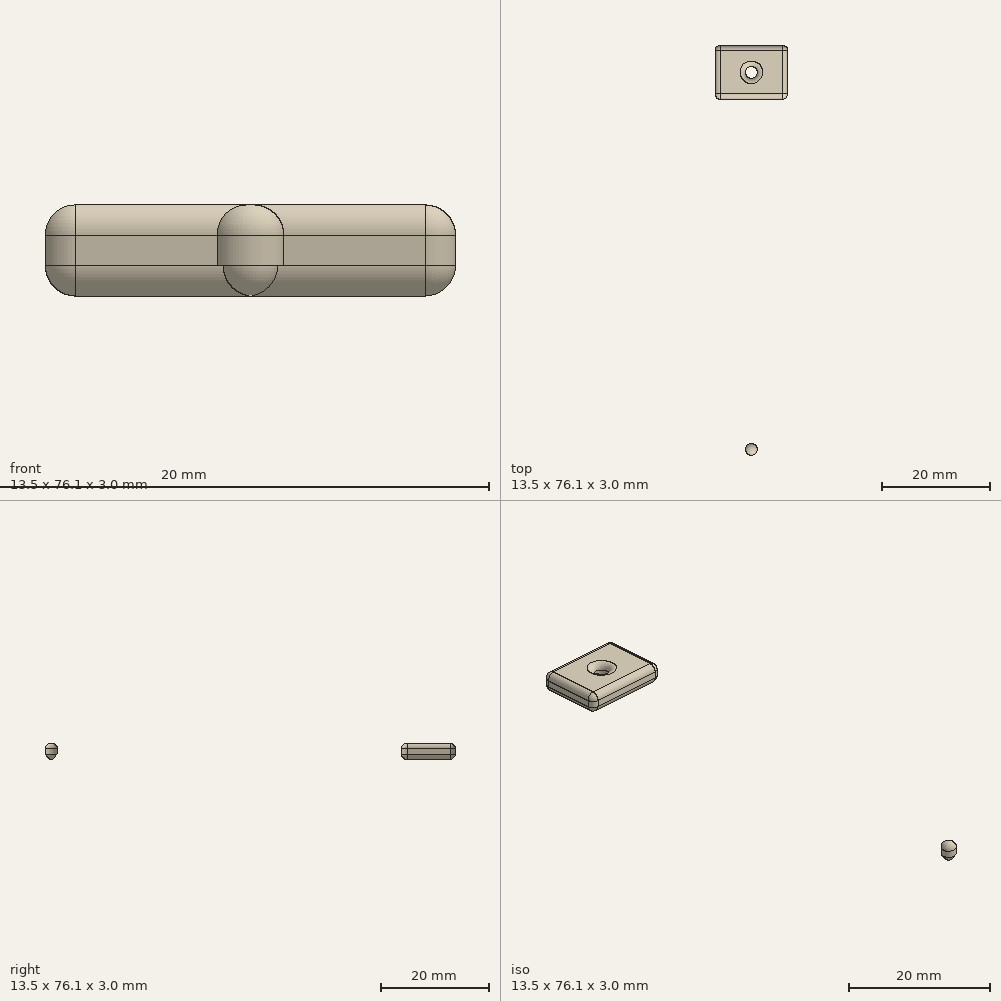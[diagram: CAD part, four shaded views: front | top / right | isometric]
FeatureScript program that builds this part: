
annotation { "Feature Type Name" : "Feature", "Feature Type Description" : "" }
export const myFeature = defineFeature(function(context is Context, id is Id, definition is map)
    precondition{}
    {
        {
            var Q0;
            Q0=qCreatedBy(makeId("Front.planeOp"),FACE);
            var sketch = newSketch(context, id + "F0", { "sketchPlane" : qUnion([Q0])});
            skLineSegment(sketch, "E0.bottom", {"start": v(-22.83, -12.2) * mm, "end": v(-9.33, -12.2) * mm});
            skLineSegment(sketch, "E0.top", {"start": v(-22.83, -9.2) * mm, "end": v(-9.33, -9.2) * mm});
            skLineSegment(sketch, "E0.left", {"start": v(-22.83, -12.2) * mm, "end": v(-22.83, -9.2) * mm});
            skLineSegment(sketch, "E0.right", {"start": v(-9.33, -12.2) * mm, "end": v(-9.33, -9.2) * mm});
            skSolve(sketch);
        }
        {
            var Q0;
            Q0=makeQuery(id+"F0.imprint","IMPRINT",FACE,{"disambiguationData":[TD([[makeQuery(id+"F0.imprint","IMPRINT",EDGE,{"derivedFrom":sQuery(id+"F0.wireOp",EDGE,"E0.bottom")}),1.0]])]});
            extrude(context, id + "F1", {"entities" : qUnion([Q0]), "depth" : 80 * mm});
        }
        {
            var Q0;
            Q0=makeQuery(id+"F1.opExtrude","SWEPT_FACE",FACE,{"disambiguationData":[OSD([sQuery(id+"F0.wireOp",EDGE,"E0.top")])]});
            var sketch = newSketch(context, id + "F2", { "sketchPlane" : qUnion([Q0])});
            skLineSegment(sketch, "E1", {"start": v(-22.83, -10) * mm, "end": v(-9.33, -10) * mm});
            skLineSegment(sketch, "E2", {"start": v(-22.83, -10) * mm, "end": v(-9.33, 0) * mm, "construction": true});
            skLineSegment(sketch, "E3", {"start": v(-9.33, -10) * mm, "end": v(-16.08, -5) * mm, "construction": true});
            skCircle(sketch, "E4", {"center": v(-16.08, -5) * mm, "radius": 1.1 * mm});
            skLineSegment(sketch, "E5", {"start": v(-9.33, 0) * mm, "end": v(-9.33, -40) * mm, "construction": true});
            skLineSegment(sketch, "E6", {"start": v(-9.33, -40) * mm, "end": v(-22.83, -40) * mm, "construction": true});
            skCircle(sketch, "E7.MirrorC", {"center": v(-16.08, -75) * mm, "radius": 1.1 * mm});
            skSolve(sketch);
        }
        {
            var Q0;
            Q0=makeQuery(id+"F2.imprint","IMPRINT",FACE,{"disambiguationData":[TD([[makeQuery(id+"F2.imprint","IMPRINT",EDGE,{"derivedFrom":sQuery(id+"F2.wireOp",EDGE,"E4")}),1.0]])]});
            var Q1;
            Q1=makeQuery(id+"F1.opExtrude","SWEPT_FACE",FACE,{"disambiguationData":[OSD([sQuery(id+"F0.wireOp",EDGE,"E0.bottom")])]});
            var Q2;
            Q2=makeQuery(id+"F2.imprint","IMPRINT",FACE,{"disambiguationData":[TD([[makeQuery(id+"F2.imprint","IMPRINT",EDGE,{"derivedFrom":sQuery(id+"F2.wireOp",EDGE,"E7.MirrorC")}),-1.0]])]});
            var Q3;
            Q3=sQuery(id+"F2.wireOp",EDGE,"E4");
            extrude(context, id + "F3", {"entities" : qUnion([Q0, Q1, Q2]), "operationType" : NewBodyOperationType.REMOVE, "surfaceEntities" : qUnion([Q3]), "oppositeDirection" : true, "depth" : 23 * mm});
        }
        {
            var Q0;
            Q0=makeQuery(id+"F1.opExtrude","SWEPT_FACE",FACE,{"disambiguationData":[OSD([sQuery(id+"F0.wireOp",EDGE,"E0.top")])]});
            var Q1;
            Q1=makeQuery(id+"F1.opExtrude","SWEPT_FACE",FACE,{"disambiguationData":[OSD([sQuery(id+"F0.wireOp",EDGE,"E0.bottom")])]});
            var Q2;
            Q2=makeQuery(id+"F1.opExtrude","SWEPT_FACE",FACE,{"disambiguationData":[OSD([sQuery(id+"F0.wireOp",EDGE,"E0.right")])]});
            var Q3;
            Q3=makeQuery(id+"F1.opExtrude","CAP_FACE",FACE,{"disambiguationData":[OSD([sQuery(id+"F0.wireOp",EDGE,"E0.bottom"),sQuery(id+"F0.wireOp",EDGE,"E0.top"),sQuery(id+"F0.wireOp",EDGE,"E0.left"),sQuery(id+"F0.wireOp",EDGE,"E0.right")])],"isStart":true});
            var Q4;
            Q4=makeQuery(id+"F1.opExtrude","SWEPT_FACE",FACE,{"disambiguationData":[OSD([sQuery(id+"F0.wireOp",EDGE,"E0.left")])]});
            fillet(context, id + "F4", {"entities" : qUnion([Q0, Q1, Q2, Q3, Q4]), "radius" : 1 * mm, "tangentPropagation" : true, "allowEdgeOverflow" : false});
        }
    });
